# Revit family: 3031606
name_source: partatom
category: Lighting Fixtures
revit_build: Autodesk Revit 2018 (Build: 20170223_1515(x64)
units: mm (PartAtom-declared; Revit-internal decimal feet)

## family parameters
Cut with Voids When Loaded = No
Host = Face
Light Source = Yes
OmniClass Number = 23.80.70.11.17
OmniClass Title = Specialized Lighting by Location or Use
Part Type = Normal
Room Calculation Point = No
Round Connector Dimension = Use Diameter
Shared = No

## types (1)
- 3031606 SYL-LIGHTER 110 LED 12W WW DIM
    Accessory Diameter = 220 mm  [stored 0.721785 ft]
    Accessory Material = Aluminum_Sylvania_Syl-Lighter LED_White
    Accessory Radius = 110 mm  [stored 0.360892 ft]
    Apparent Load = 12 VA
    Assembly Code = D5020200
    Beam Angle = 74.00°
    Body Material = Metal_Sylvania_Syl-Lighter LED_Silver
    CRI ( Ra ) = 80
    Catalog Number = 3031605 Syl-Lighter 220 LED 21W NW
    Color Filter = 16777215
    Cutout Diameter = 200 mm  [stored 0.656168 ft]
    Default Elevation = 0 mm  [stored 0 ft]
    Description = Syl-lighter Round is available in 3 different body sizes: 165mm, 195mm & 220mm. High lumen output - up to 1,742lm. High efficiency - up to 80.9lm. Choice of 3,000K warm white or 4,000K neutral white colour temperature. Small recessed depth (<60mm)
    Diameter = 200 mm  [stored 0.656168 ft]
    Diffuser Diameter = 180 mm  [stored 0.590551 ft]
    Diffuser Material = Polycarbonate_Sylvania_Syl-Lighter LED_Opal
    Diffuser Radius = 90 mm  [stored 0.295276 ft]
    Dimming Lamp Color Temperature Shift = <None>
    Drive Current = 500mA
    Electrical Protection = CLASS II
    Emit Shape Visible in Rendering = No
    Emit from Circle Diameter = 180 mm  [stored 0.590551 ft]
    Glow Wire Test = 960 °C
    Height = 60 mm  [stored 0.19685 ft]
    IK Rating = IK02
    IP Rating = IP44
    Inner Diameter = 196 mm  [stored 0.643045 ft]
    LOR = 1
    Lamp Comments = Integrated LED
    Life = 50 000
    Model = SYL-LIGHTER 110 LED 12W WW DIM
    Photometric Web File = 3031606.ies
    Product Family = SYL-LIGHTER LED ROUND - 4,000K LAMP
    Recessed Depth = 60 mm  [stored 0.19685 ft]
    T Class Max = -1 °C
    T Class Min = -1 °C
    Tilt Angle = -90.00°
    URL = 0
    Voltage = 240 V
    Voltage Comments = UNV (Universal Voltage; 220-240 Volt)
    Weight = 1.10 kg

note: [stored X ft] marks values corroborated as IEEE doubles in the binary element streams (Revit-internal decimal feet)

## geometry (parser evidence)
native form markers: Blend x6, Sweep x2
no freeform markers — native parametric forms only
